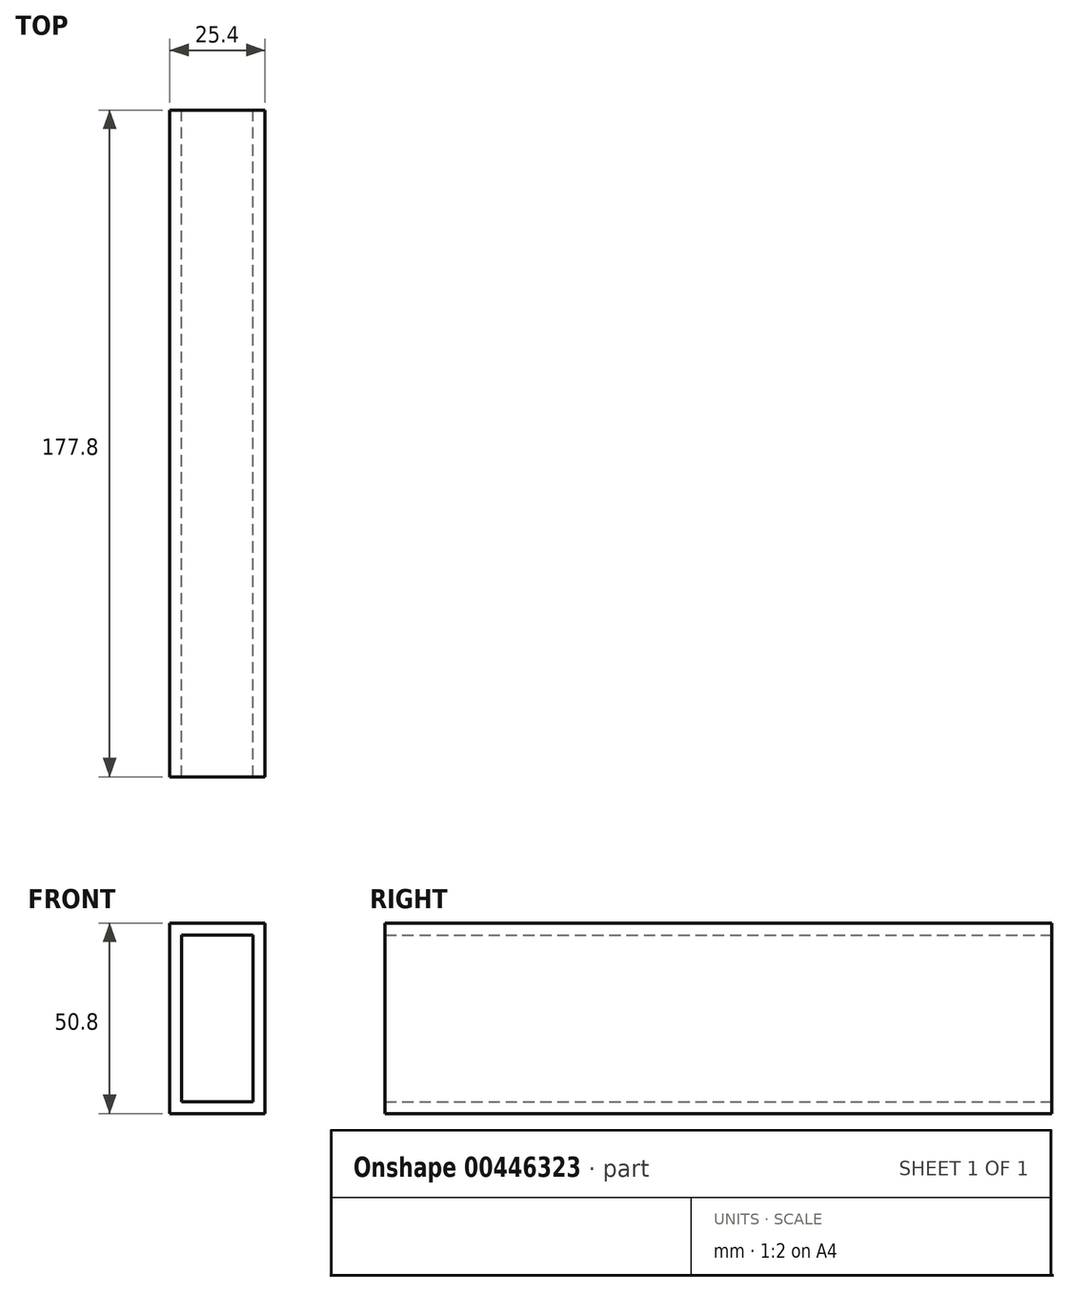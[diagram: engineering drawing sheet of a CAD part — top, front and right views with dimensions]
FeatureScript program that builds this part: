
annotation { "Feature Type Name" : "Feature", "Feature Type Description" : "" }
export const myFeature = defineFeature(function(context is Context, id is Id, definition is map)
    precondition{}
    {
        {
            var Q0;
            Q0=qCreatedBy(makeId("Front.planeOp"),FACE);
            var sketch = newSketch(context, id + "F0", { "sketchPlane" : qUnion([Q0])});
            skLineSegment(sketch, "E0.bottom", {"start": v(9.53, 22.23) * mm, "end": v(-9.52, 22.23) * mm});
            skLineSegment(sketch, "E0.top", {"start": v(9.53, -22.23) * mm, "end": v(-9.52, -22.23) * mm});
            skLineSegment(sketch, "E0.left", {"start": v(9.53, 22.23) * mm, "end": v(9.53, -22.23) * mm});
            skLineSegment(sketch, "E0.right", {"start": v(-9.52, 22.23) * mm, "end": v(-9.52, -22.23) * mm});
            skPoint(sketch, "E0.middle", {"position": v(0, 0) * mm});
            skLineSegment(sketch, "E1.0", {"start": v(12.7, 25.4) * mm, "end": v(-12.7, 25.4) * mm});
            skLineSegment(sketch, "E1.1", {"start": v(12.7, 25.4) * mm, "end": v(12.7, -25.4) * mm});
            skLineSegment(sketch, "E1.2", {"start": v(12.7, -25.4) * mm, "end": v(-12.7, -25.4) * mm});
            skLineSegment(sketch, "E1.3", {"start": v(-12.7, 25.4) * mm, "end": v(-12.7, -25.4) * mm});
            skSolve(sketch);
        }
        {
            var Q0;
            Q0=makeQuery(id+"F0.imprint","IMPRINT",FACE,{"disambiguationData":[TD([[makeQuery(id+"F0.imprint","IMPRINT",EDGE,{"derivedFrom":sQuery(id+"F0.wireOp",EDGE,"E0.bottom")}),-1.0]])]});
            extrude(context, id + "F1", {"entities" : qUnion([Q0]), "depth" : 177.8 * mm, "offsetDistance" : 25.4 * mm, "symmetric" : true});
        }
    });
